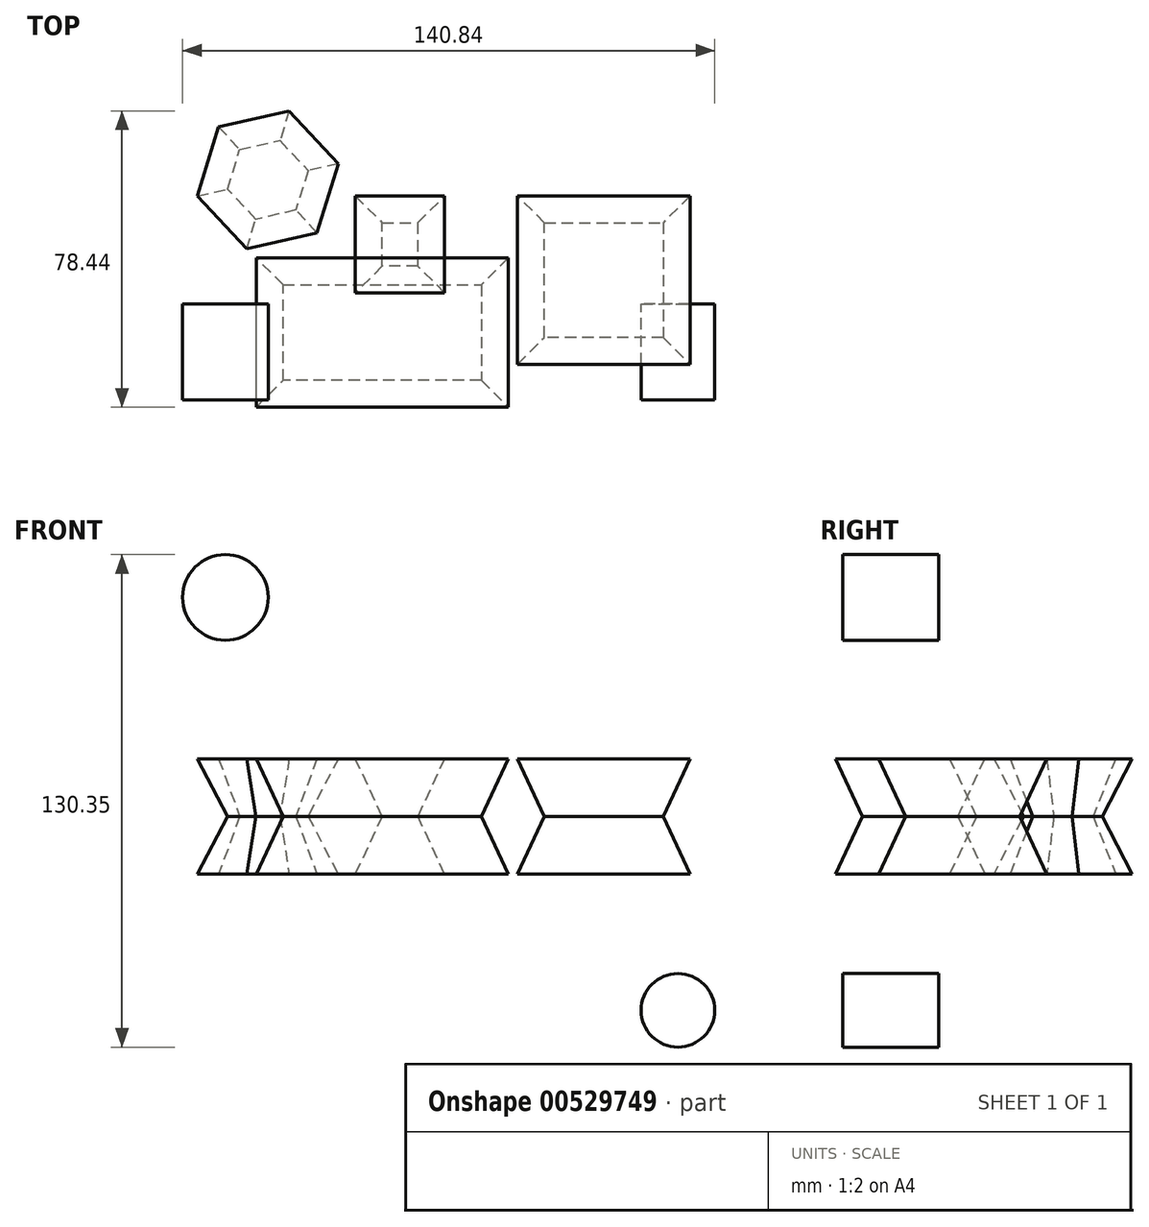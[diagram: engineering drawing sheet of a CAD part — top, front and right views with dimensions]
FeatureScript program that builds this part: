
annotation { "Feature Type Name" : "Feature", "Feature Type Description" : "" }
export const myFeature = defineFeature(function(context is Context, id is Id, definition is map)
    precondition{}
    {
        {
            var Q0;
            Q0=qCreatedBy(makeId("Top.planeOp"),FACE);
            var sketch = newSketch(context, id + "F0", { "sketchPlane" : qUnion([Q0])});
            skLineSegment(sketch, "E0.bottom", {"start": v(-55.08, 5.12) * mm, "end": v(-2.57, 5.12) * mm});
            skLineSegment(sketch, "E0.top", {"start": v(-55.08, -20.18) * mm, "end": v(-2.57, -20.18) * mm});
            skLineSegment(sketch, "E0.left", {"start": v(-55.08, 5.12) * mm, "end": v(-55.08, -20.18) * mm});
            skLineSegment(sketch, "E0.right", {"start": v(-2.57, 5.12) * mm, "end": v(-2.57, -20.18) * mm});
            skPoint(sketch, "E1.firstSnap0", {"position": v(-28.82, 5.12) * mm});
            skLineSegment(sketch, "E1.bottom", {"start": v(-28.82, 10.07) * mm, "end": v(-19.41, 10.07) * mm});
            skLineSegment(sketch, "E1.top", {"start": v(-28.82, 21.52) * mm, "end": v(-19.41, 21.52) * mm});
            skLineSegment(sketch, "E1.left", {"start": v(-28.82, 10.07) * mm, "end": v(-28.82, 21.52) * mm});
            skLineSegment(sketch, "E1.right", {"start": v(-19.41, 10.07) * mm, "end": v(-19.41, 21.52) * mm});
            skLineSegment(sketch, "E2.bottom", {"start": v(14.08, 21.52) * mm, "end": v(45.5, 21.52) * mm});
            skLineSegment(sketch, "E2.top", {"start": v(14.08, -8.8) * mm, "end": v(45.5, -8.8) * mm});
            skLineSegment(sketch, "E2.left", {"start": v(14.08, 21.52) * mm, "end": v(14.08, -8.8) * mm});
            skLineSegment(sketch, "E2.right", {"start": v(45.5, 21.52) * mm, "end": v(45.5, -8.8) * mm});
            skCircle(sketch, "E3.cCircle", {"center": v(-59.1, 32.88) * mm, "radius": 9.45 * mm, "construction": true});
            skLineSegment(sketch, "E3.0", {"start": v(-48.47, 35.31) * mm, "end": v(-51.68, 24.88) * mm});
            skLineSegment(sketch, "E3.1", {"start": v(-51.68, 24.88) * mm, "end": v(-62.32, 22.45) * mm});
            skLineSegment(sketch, "E3.2", {"start": v(-62.32, 22.45) * mm, "end": v(-69.75, 30.45) * mm});
            skLineSegment(sketch, "E3.3", {"start": v(-69.75, 30.45) * mm, "end": v(-66.53, 40.88) * mm});
            skLineSegment(sketch, "E3.4", {"start": v(-66.53, 40.88) * mm, "end": v(-55.9, 43.31) * mm});
            skLineSegment(sketch, "E3.5", {"start": v(-55.9, 43.31) * mm, "end": v(-48.47, 35.31) * mm});
            skPoint(sketch, "E3.0.midPoint", {"position": v(-50.07, 30.1) * mm});
            skSolve(sketch);
        }
        {
            var Q0;
            Q0 = qSketchRegion(id + "F0", true);
            extrude(context, id + "F1", {"entities" : qUnion([Q0]), "depth" : 15.24 * mm, "offsetDistance" : 25.4 * mm, "hasDraft" : true, "draftAngle" : 25 * degree, "hasSecondDirection" : true, "secondDirectionOppositeDirection" : true, "secondDirectionDepth" : 15.24 * mm, "hasSecondDirectionDraft" : true, "secondDirectionDraftAngle" : 25 * degree});
        }
        {
            var Q0;
            Q0=qCreatedBy(makeId("Front.planeOp"),FACE);
            var sketch = newSketch(context, id + "F2", { "sketchPlane" : qUnion([Q0])});
            skCircle(sketch, "E4", {"center": v(-70.35, 57.92) * mm, "radius": 11.33 * mm});
            skCircle(sketch, "E5", {"center": v(49.43, -51.37) * mm, "radius": 9.73 * mm});
            skSolve(sketch);
        }
        {
            var Q0;
            Q0=makeQuery(id+"F2.imprint","IMPRINT",FACE,{"disambiguationData":[TD([[makeQuery(id+"F2.imprint","IMPRINT",EDGE,{"derivedFrom":sQuery(id+"F2.wireOp",EDGE,"E4")}),1.0]])]});
            var Q1;
            Q1=makeQuery(id+"F2.imprint","IMPRINT",FACE,{"disambiguationData":[TD([[makeQuery(id+"F2.imprint","IMPRINT",EDGE,{"derivedFrom":sQuery(id+"F2.wireOp",EDGE,"E5")}),1.0]])]});
            extrude(context, id + "F3", {"entities" : qUnion([Q0, Q1]), "depth" : 25.4 * mm, "offsetDistance" : 25.4 * mm});
        }
    });
